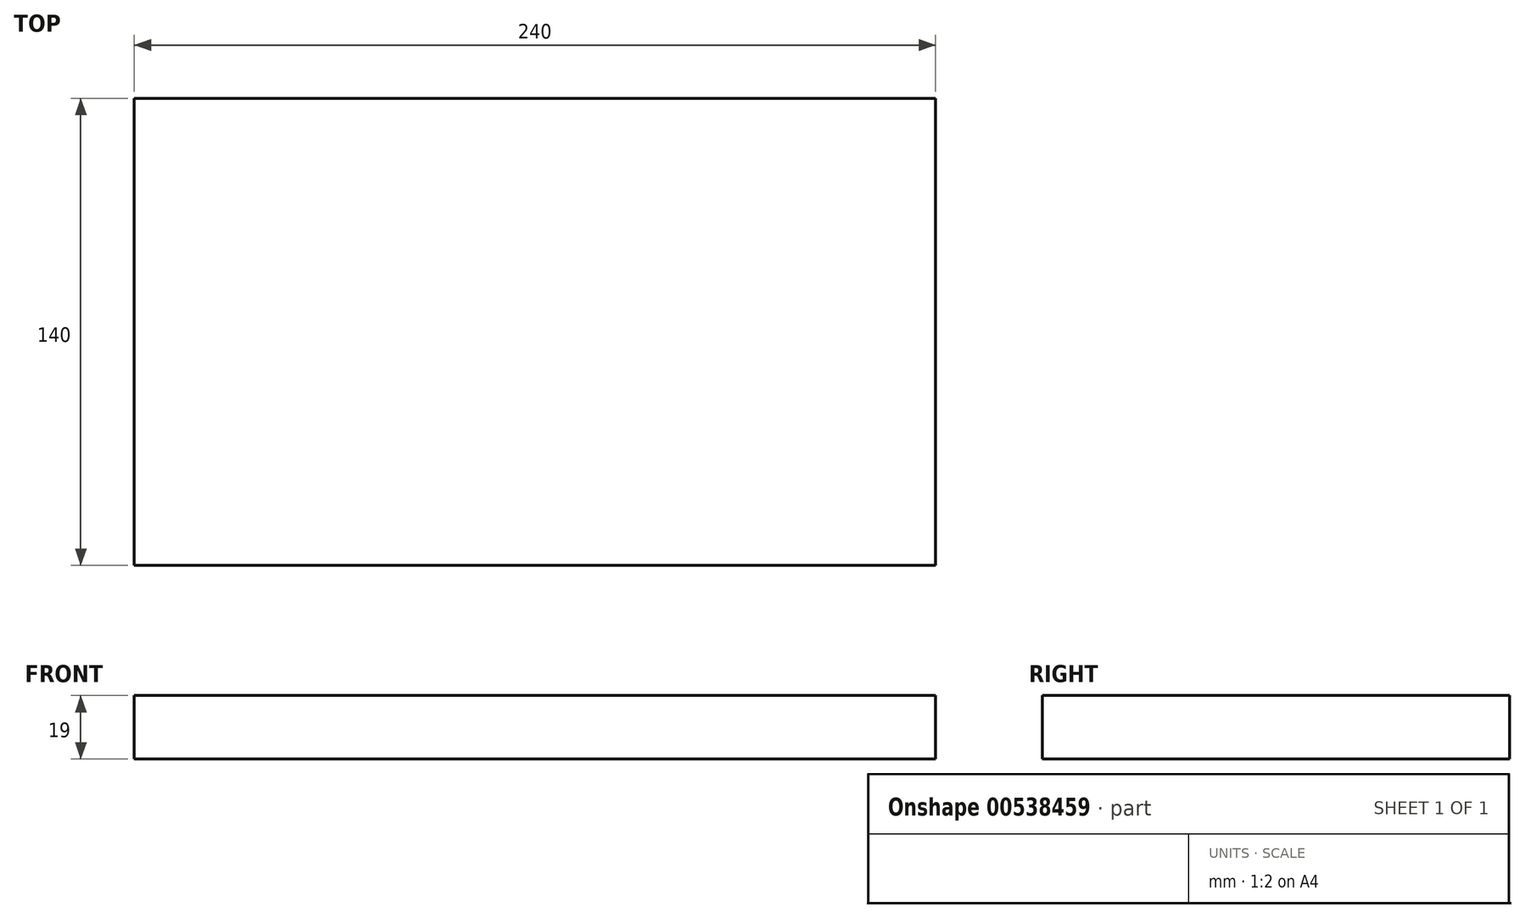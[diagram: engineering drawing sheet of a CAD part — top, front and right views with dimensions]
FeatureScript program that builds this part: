
annotation { "Feature Type Name" : "Feature", "Feature Type Description" : "" }
export const myFeature = defineFeature(function(context is Context, id is Id, definition is map)
    precondition{}
    {
        {
            var Q0;
            Q0=qCreatedBy(makeId("Top.planeOp"),FACE);
            var sketch = newSketch(context, id + "F0", { "sketchPlane" : qUnion([Q0])});
            skLineSegment(sketch, "E0.bottom", {"start": v(-157.17, 50.71) * mm, "end": v(82.83, 50.71) * mm});
            skLineSegment(sketch, "E0.top", {"start": v(-157.17, -89.29) * mm, "end": v(82.83, -89.29) * mm});
            skLineSegment(sketch, "E0.left", {"start": v(-157.17, 50.71) * mm, "end": v(-157.17, -89.29) * mm});
            skLineSegment(sketch, "E0.right", {"start": v(82.83, 50.71) * mm, "end": v(82.83, -89.29) * mm});
            skSolve(sketch);
        }
        {
            var Q0;
            Q0 = qSketchRegion(id + "F0", true);
            extrude(context, id + "F1", {"entities" : qUnion([Q0]), "depth" : 19 * mm, "offsetDistance" : 25 * mm});
        }
    });
